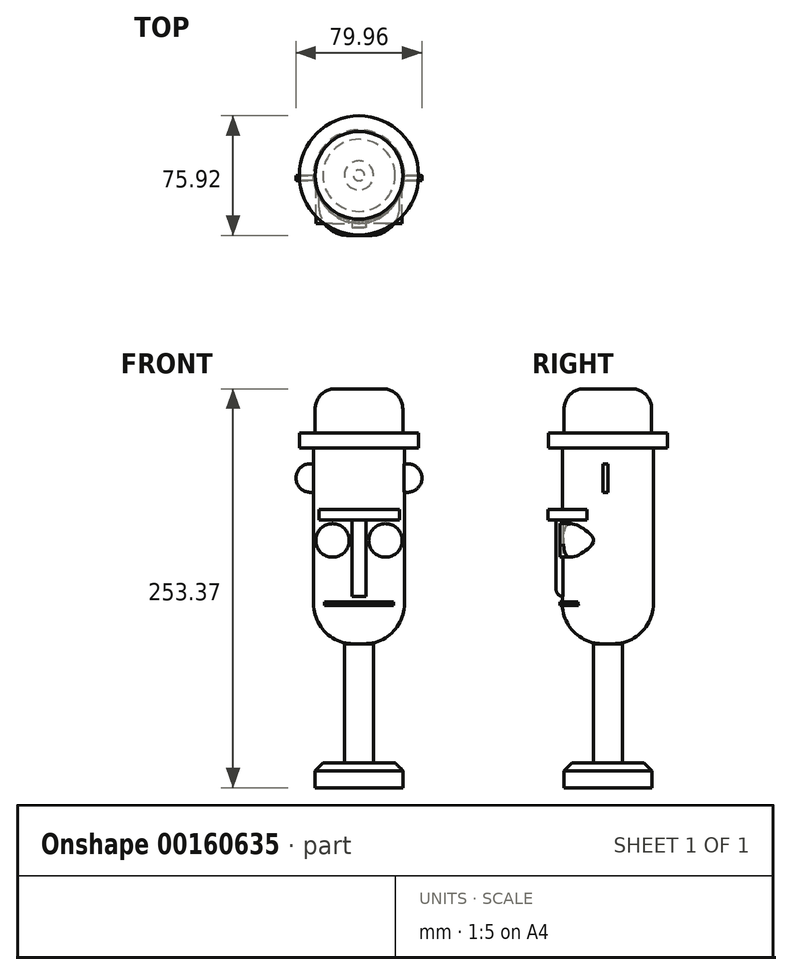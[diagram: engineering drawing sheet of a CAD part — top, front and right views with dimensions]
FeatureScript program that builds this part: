
annotation { "Feature Type Name" : "Feature", "Feature Type Description" : "" }
export const myFeature = defineFeature(function(context is Context, id is Id, definition is map)
    precondition{}
    {
        {
            var Q0;
            Q0=qCreatedBy(makeId("Top.planeOp"),FACE);
            var sketch = newSketch(context, id + "F0", { "sketchPlane" : qUnion([Q0])});
            skCircle(sketch, "E0", {"center": v(0, 0) * mm, "radius": 28.9 * mm});
            skSolve(sketch);
        }
        {
            var Q0;
            Q0=makeQuery(id+"F0.imprint","IMPRINT",FACE,{"disambiguationData":[TD([[makeQuery(id+"F0.imprint","IMPRINT",EDGE,{"derivedFrom":sQuery(id+"F0.wireOp",EDGE,"E0")}),1.0]])]});
            extrude(context, id + "F1", {"entities" : qUnion([Q0]), "depth" : 132.08 * mm});
        }
        {
            var Q0;
            Q0=makeQuery(id+"F1.opExtrude","CAP_EDGE",EDGE,{"disambiguationData":[OSD([sQuery(id+"F0.wireOp",EDGE,"E0")])],"isStart":true});
            fillet(context, id + "F2", {"entities" : qUnion([Q0]), "radius" : 25.4 * mm, "tangentPropagation" : true, "allowEdgeOverflow" : false});
        }
        {
            var Q0;
            Q0=qCreatedBy(makeId("Top.planeOp"),FACE);
            var sketch = newSketch(context, id + "F3", { "sketchPlane" : qUnion([Q0])});
            skCircle(sketch, "E1", {"center": v(0, 0) * mm, "radius": 9.25 * mm});
            skSolve(sketch);
        }
        {
            var Q0;
            Q0 = qSketchRegion(id + "F3", true);
            extrude(context, id + "F4", {"entities" : qUnion([Q0]), "operationType" : NewBodyOperationType.ADD, "oppositeDirection" : true, "depth" : 83.18 * mm});
        }
        {
            var Q0;
            Q0=qCreatedBy(makeId("Front.planeOp"),FACE);
            var sketch = newSketch(context, id + "F5", { "sketchPlane" : qUnion([Q0])});
            skCircle(sketch, "E2", {"center": v(30.92, 105.26) * mm, "radius": 9.07 * mm});
            skCircle(sketch, "E3.MirrorC", {"center": v(-30.92, 105.26) * mm, "radius": 9.07 * mm});
            skSolve(sketch);
        }
        {
            var Q0;
            Q0 = qSketchRegion(id + "F5", true);
            extrude(context, id + "F6", {"entities" : qUnion([Q0]), "operationType" : NewBodyOperationType.ADD, "depth" : 3.17 * mm});
        }
        {
            var Q0;
            Q0=qCreatedBy(makeId("Front.planeOp"),FACE);
            var sketch = newSketch(context, id + "F7", { "sketchPlane" : qUnion([Q0])});
            skLineSegment(sketch, "E4.bottom", {"start": v(4.39, 79.96) * mm, "end": v(-4.39, 79.96) * mm});
            skLineSegment(sketch, "E4.top", {"start": v(4.39, 29.94) * mm, "end": v(-4.39, 29.94) * mm});
            skLineSegment(sketch, "E4.left", {"start": v(4.39, 79.96) * mm, "end": v(4.39, 29.94) * mm});
            skLineSegment(sketch, "E4.right", {"start": v(-4.39, 79.96) * mm, "end": v(-4.39, 29.94) * mm});
            skPoint(sketch, "E4.middle", {"position": v(0, 54.95) * mm});
            skSolve(sketch);
        }
        {
            var Q0;
            Q0 = qSketchRegion(id + "F7", true);
            extrude(context, id + "F8", {"entities" : qUnion([Q0]), "operationType" : NewBodyOperationType.ADD, "depth" : 33.02 * mm});
        }
        {
            var Q0;
            Q0=qCreatedBy(makeId("Front.planeOp"),FACE);
            var sketch = newSketch(context, id + "F9", { "sketchPlane" : qUnion([Q0])});
            skLineSegment(sketch, "E5.bottom", {"start": v(-25.32, 78.72) * mm, "end": v(25.69, 78.72) * mm});
            skLineSegment(sketch, "E5.top", {"start": v(-25.32, 85.21) * mm, "end": v(25.69, 85.21) * mm});
            skLineSegment(sketch, "E5.left", {"start": v(-25.32, 78.72) * mm, "end": v(-25.32, 85.21) * mm});
            skLineSegment(sketch, "E5.right", {"start": v(25.69, 78.72) * mm, "end": v(25.69, 85.21) * mm});
            skSolve(sketch);
        }
        {
            var Q0;
            Q0 = qSketchRegion(id + "F9", true);
            extrude(context, id + "F10", {"entities" : qUnion([Q0]), "operationType" : NewBodyOperationType.ADD, "depth" : 38.1 * mm});
        }
        {
            var Q0;
            Q0=qCreatedBy(makeId("Front.planeOp"),FACE);
            var sketch = newSketch(context, id + "F11", { "sketchPlane" : qUnion([Q0])});
            skCircle(sketch, "E6", {"center": v(16.8, 65.62) * mm, "radius": 10.63 * mm});
            skCircle(sketch, "E7.MirrorC", {"center": v(-16.8, 65.62) * mm, "radius": 10.63 * mm});
            skSolve(sketch);
        }
        {
            var Q0;
            Q0 = qSketchRegion(id + "F11", true);
            extrude(context, id + "F12", {"entities" : qUnion([Q0]), "operationType" : NewBodyOperationType.ADD, "depth" : 30.48 * mm});
        }
        {
            var Q0;
            Q0=qCreatedBy(makeId("Top.planeOp"),FACE);
            var sketch = newSketch(context, id + "F13", { "sketchPlane" : qUnion([Q0])});
            skCircle(sketch, "E8", {"center": v(0, 0) * mm, "radius": 37.82 * mm});
            skSolve(sketch);
        }
        {
            var Q0;
            Q0 = qSketchRegion(id + "F13", true);
            extrude(context, id + "F14", {"entities" : qUnion([Q0]), "operationType" : NewBodyOperationType.ADD, "depth" : 133.98 * mm, "hasSecondDirection" : true, "secondDirectionOppositeDirection" : false, "secondDirectionDepth" : 124.46 * mm});
        }
        {
            var Q0;
            Q0=qCreatedBy(makeId("Top.planeOp"),FACE);
            var sketch = newSketch(context, id + "F15", { "sketchPlane" : qUnion([Q0])});
            skCircle(sketch, "E9", {"center": v(0, 0) * mm, "radius": 27.82 * mm});
            skSolve(sketch);
        }
        {
            var Q0;
            Q0 = qSketchRegion(id + "F15", true);
            extrude(context, id + "F16", {"entities" : qUnion([Q0]), "operationType" : NewBodyOperationType.ADD, "depth" : 161.92 * mm, "hasSecondDirection" : true, "secondDirectionOppositeDirection" : false, "secondDirectionDepth" : 120.65 * mm});
        }
        {
            var Q0;
            Q0=makeQuery(id+"F16.opExtrude","CAP_EDGE",EDGE,{"disambiguationData":[OSD([sQuery(id+"F15.wireOp",EDGE,"E9")])],"isStart":false});
            fillet(context, id + "F17", {"entities" : qUnion([Q0]), "radius" : 12.7 * mm, "tangentPropagation" : true, "allowEdgeOverflow" : false});
        }
        {
            var Q0;
            Q0=qCreatedBy(makeId("Top.planeOp"),FACE);
            var sketch = newSketch(context, id + "F18", { "sketchPlane" : qUnion([Q0])});
            skCircle(sketch, "E10", {"center": v(0, 0) * mm, "radius": 27.96 * mm});
            skSolve(sketch);
        }
        {
            var Q0;
            Q0 = qSketchRegion(id + "F18", true);
            extrude(context, id + "F19", {"entities" : qUnion([Q0]), "operationType" : NewBodyOperationType.ADD, "oppositeDirection" : true, "depth" : 91.44 * mm, "hasSecondDirection" : true, "secondDirectionOppositeDirection" : true, "secondDirectionDepth" : 75.56 * mm});
        }
        {
            var Q0;
            Q0=makeQuery(id+"F19.opExtrude","CAP_EDGE",EDGE,{"disambiguationData":[OSD([sQuery(id+"F18.wireOp",EDGE,"E10")])],"isStart":true});
            chamfer(context, id + "F20", {"entities" : qUnion([Q0]), "width" : 5.08 * mm, "tangentPropagation" : true});
        }
        {
            var Q0;
            Q0=qCreatedBy(makeId("Front.planeOp"),FACE);
            var sketch = newSketch(context, id + "F21", { "sketchPlane" : qUnion([Q0])});
            skLineSegment(sketch, "E11.bottom", {"start": v(21.92, 24.32) * mm, "end": v(-21.92, 24.32) * mm});
            skLineSegment(sketch, "E11.top", {"start": v(21.92, 26.7) * mm, "end": v(-21.92, 26.7) * mm});
            skLineSegment(sketch, "E11.left", {"start": v(21.92, 24.32) * mm, "end": v(21.92, 26.7) * mm});
            skLineSegment(sketch, "E11.right", {"start": v(-21.92, 24.32) * mm, "end": v(-21.92, 26.7) * mm});
            skPoint(sketch, "E11.middle", {"position": v(0, 25.51) * mm});
            skSolve(sketch);
        }
        {
            var Q0;
            Q0 = qSketchRegion(id + "F21", true);
            extrude(context, id + "F22", {"entities" : qUnion([Q0]), "operationType" : NewBodyOperationType.ADD, "depth" : 30.48 * mm});
        }
        {
            var Q0;
            Q0=makeQuery(id+"F22.opExtrude","CAP_EDGE",EDGE,{"disambiguationData":[OSD([sQuery(id+"F21.wireOp",EDGE,"E11.right")])],"isStart":false});
            fillet(context, id + "F23", {"entities" : qUnion([Q0]), "radius" : 25.4 * mm, "tangentPropagation" : true, "allowEdgeOverflow" : false});
        }
        {
            var Q0;
            Q0=makeQuery(id+"F22.opExtrude","CAP_EDGE",EDGE,{"disambiguationData":[OSD([sQuery(id+"F21.wireOp",EDGE,"E11.left")])],"isStart":false});
            fillet(context, id + "F24", {"entities" : qUnion([Q0]), "radius" : 25.4 * mm, "tangentPropagation" : true, "allowEdgeOverflow" : false});
        }
        {
            var Q0;
            Q0=makeQuery(id+"F10.opExtrude","CAP_EDGE",EDGE,{"disambiguationData":[OSD([sQuery(id+"F9.wireOp",EDGE,"E5.left")])],"isStart":false});
            var Q1;
            Q1=makeQuery(id+"F10.opExtrude","CAP_EDGE",EDGE,{"disambiguationData":[OSD([sQuery(id+"F9.wireOp",EDGE,"E5.right")])],"isStart":false});
            fillet(context, id + "F25", {"entities" : qUnion([Q0, Q1]), "radius" : 17.78 * mm, "tangentPropagation" : true, "allowEdgeOverflow" : false});
        }
        {
            var Q0;
            Q0=makeQuery(id+"F8.opExtrude","CAP_EDGE",EDGE,{"disambiguationData":[OSD([sQuery(id+"F7.wireOp",EDGE,"E4.top")])],"isStart":false});
            fillet(context, id + "F26", {"entities" : qUnion([Q0]), "radius" : 5.08 * mm, "tangentPropagation" : true, "allowEdgeOverflow" : false});
        }
    });
